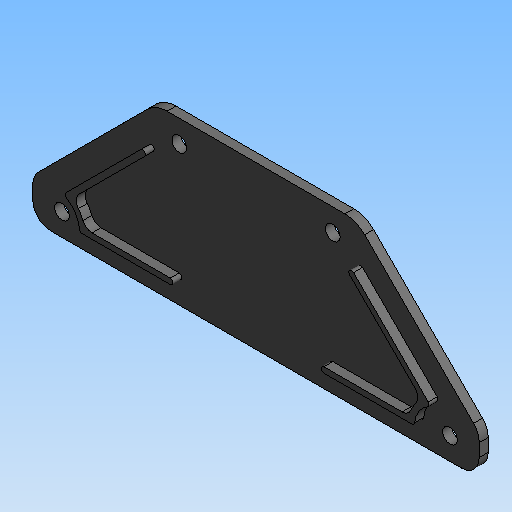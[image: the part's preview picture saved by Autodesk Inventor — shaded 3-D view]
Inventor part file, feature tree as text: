
AUTODESK INVENTOR PART (.ipt)
format: ipt  version: 2020 (Build 240168000, 168)  size: 150,528 bytes
history: native  units: mm (DEFAULTED — no unit token found)
features: other x14, extrude x3, sketch x3
ambient origin geometry x8: Origin, YZ Plane, XZ Plane, XY Plane, X Axis, Y Axis, Z Axis, Center Point
bodies: Solid1 (feature_tree)
feature tree (20):
  extrude  "Extrusion1"  Depth=3.2mm TaperAngle=0.0deg
  extrude  "Extrusion2"  TaperAngle=0.0deg  [1 undecoded]
  extrude  "Extrusion3"  [1 undecoded]
  other  "swivel_to_body_XY"
  other  "swivel_to_body_YZ"
  other  "swivel_to_body_ZX"
  other  "swivel_to_body_X"
  other  "swivel_to_body_Y"
  other  "swivel_to_body_Z"
  other  "swivel_to_body_Center"
  other  "swivel_to_dummy_XY"
  other  "swivel_to_dummy_YZ"
  other  "swivel_to_dummy_ZX"
  other  "swivel_to_dummy_X"
  other  "swivel_to_dummy_Y"
  other  "swivel_to_dummy_Z"
  other  "swivel_to_dummy_Center"
  sketch  "Sketch_1"  dims[d0=3.2mm d1=0.0mm d2=3.2mm d3=0.0mm]
  sketch  "Sketch_2"  dims[d4=3.2mm d5=0.0mm d6=0.0mm]
  sketch  "Sketch_3"
note: 2 required parameter values undecoded (feature->parameter linkage not recoverable at this tier; creation-order binding heuristic only, values carry confidence <= 0.55)
